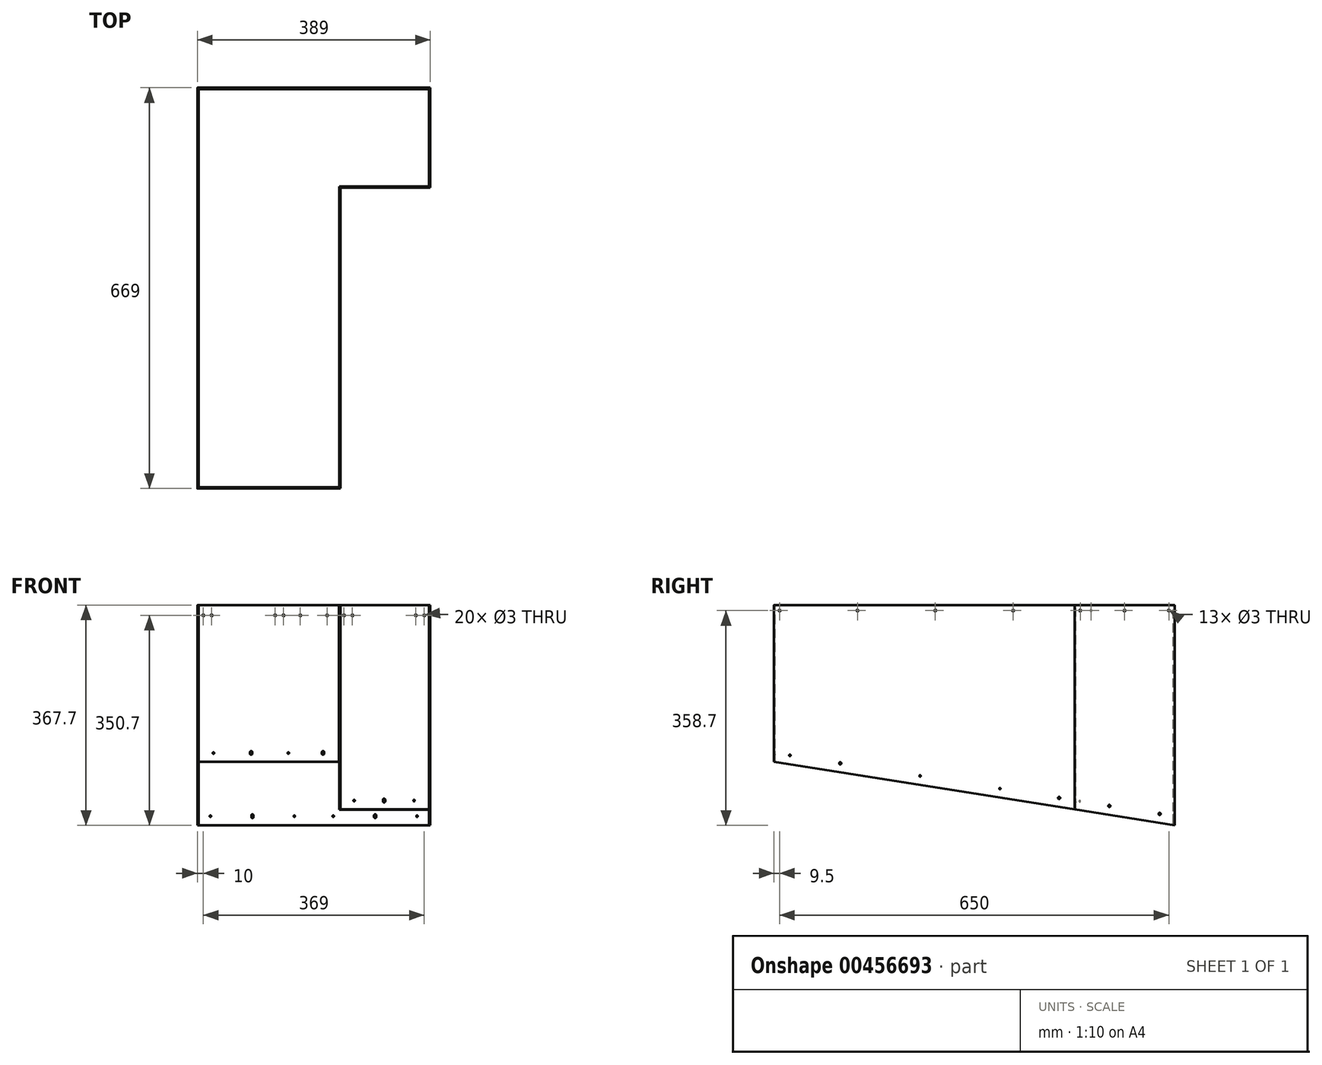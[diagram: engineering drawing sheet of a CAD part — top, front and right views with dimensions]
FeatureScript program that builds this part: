
annotation { "Feature Type Name" : "Feature", "Feature Type Description" : "" }
export const myFeature = defineFeature(function(context is Context, id is Id, definition is map)
    precondition{}
    {
        {
            var Q0;
            Q0=qCreatedBy(makeId("Top.planeOp"),FACE);
            var sketch = newSketch(context, id + "F0", { "sketchPlane" : qUnion([Q0])});
            skLineSegment(sketch, "E0.bottom", {"start": v(192.25, 332.5) * mm, "end": v(-192.25, 332.5) * mm});
            skLineSegment(sketch, "E0.top", {"start": v(192.25, 334.5) * mm, "end": v(-192.25, 334.5) * mm});
            skLineSegment(sketch, "E0.left", {"start": v(192.25, 332.5) * mm, "end": v(192.25, 334.5) * mm});
            skLineSegment(sketch, "E0.right", {"start": v(-192.25, 332.5) * mm, "end": v(-192.25, 334.5) * mm});
            skPoint(sketch, "E0.middle", {"position": v(0, 333.5) * mm});
            skSolve(sketch);
        }
        {
            var Q0;
            Q0=qSketchRegion(id+"F0",true);
            extrude(context, id + "F1", {"entities" : qUnion([Q0]), "oppositeDirection" : true, "depth" : 367.4 * mm});
        }
        {
            var Q0;
            Q0=qCreatedBy(makeId("Top.planeOp"),FACE);
            var sketch = newSketch(context, id + "F2", { "sketchPlane" : qUnion([Q0])});
            skLineSegment(sketch, "E1.bottom", {"start": v(-192.25, -332.5) * mm, "end": v(42.25, -332.5) * mm});
            skLineSegment(sketch, "E1.top", {"start": v(-192.25, -334.5) * mm, "end": v(42.25, -334.5) * mm});
            skLineSegment(sketch, "E1.left", {"start": v(-192.25, -332.5) * mm, "end": v(-192.25, -334.5) * mm});
            skLineSegment(sketch, "E1.right", {"start": v(42.25, -332.5) * mm, "end": v(42.25, -334.5) * mm});
            skSolve(sketch);
        }
        {
            var Q0;
            Q0=qSketchRegion(id+"F2",true);
            extrude(context, id + "F3", {"entities" : qUnion([Q0]), "oppositeDirection" : true, "depth" : 261.8 * mm});
        }
        {
            var Q0;
            Q0=qCreatedBy(makeId("Top.planeOp"),FACE);
            var sketch = newSketch(context, id + "F4", { "sketchPlane" : qUnion([Q0])});
            skLineSegment(sketch, "E2.bottom", {"start": v(42.75, 169.5) * mm, "end": v(192.25, 169.5) * mm});
            skLineSegment(sketch, "E2.top", {"start": v(42.75, 167.5) * mm, "end": v(192.25, 167.5) * mm});
            skLineSegment(sketch, "E2.left", {"start": v(42.75, 169.5) * mm, "end": v(42.75, 167.5) * mm});
            skLineSegment(sketch, "E2.right", {"start": v(192.25, 169.5) * mm, "end": v(192.25, 167.5) * mm});
            skSolve(sketch);
        }
        {
            var Q0;
            Q0=qSketchRegion(id+"F4",true);
            extrude(context, id + "F5", {"entities" : qUnion([Q0]), "oppositeDirection" : true, "depth" : 341.3 * mm});
        }
        {
            var Q0;
            Q0=qCreatedBy(makeId("Top.planeOp"),FACE);
            var sketch = newSketch(context, id + "F6", { "sketchPlane" : qUnion([Q0])});
            skLineSegment(sketch, "E3.bottom", {"start": v(-192.5, -334.5) * mm, "end": v(-194.5, -334.5) * mm});
            skLineSegment(sketch, "E3.top", {"start": v(-192.5, 334.5) * mm, "end": v(-194.5, 334.5) * mm});
            skLineSegment(sketch, "E3.left", {"start": v(-192.5, -334.5) * mm, "end": v(-192.5, 334.5) * mm});
            skLineSegment(sketch, "E3.right", {"start": v(-194.5, -334.5) * mm, "end": v(-194.5, 334.5) * mm});
            skPoint(sketch, "E3.middle", {"position": v(-193.5, 0) * mm});
            skLineSegment(sketch, "E4.bottom", {"start": v(42.5, 167.5) * mm, "end": v(44.5, 167.5) * mm});
            skLineSegment(sketch, "E4.top", {"start": v(42.5, -334.5) * mm, "end": v(44.5, -334.5) * mm});
            skLineSegment(sketch, "E4.left", {"start": v(42.5, 167.5) * mm, "end": v(42.5, -334.5) * mm});
            skLineSegment(sketch, "E4.right", {"start": v(44.5, 167.5) * mm, "end": v(44.5, -334.5) * mm});
            skLineSegment(sketch, "E5.bottom", {"start": v(192.5, 334.5) * mm, "end": v(194.5, 334.5) * mm});
            skLineSegment(sketch, "E5.top", {"start": v(192.5, 167.5) * mm, "end": v(194.5, 167.5) * mm});
            skLineSegment(sketch, "E5.left", {"start": v(192.5, 334.5) * mm, "end": v(192.5, 167.5) * mm});
            skLineSegment(sketch, "E5.right", {"start": v(194.5, 334.5) * mm, "end": v(194.5, 167.5) * mm});
            skSolve(sketch);
        }
        {
            var Q0;
            Q0=qSketchRegion(id+"F6",true);
            extrude(context, id + "F7", {"entities" : qUnion([Q0]), "oppositeDirection" : true, "depth" : 388 * mm});
        }
        {
            var Q0;
            Q0=makeQuery(id+"F1.opExtrude","SWEPT_FACE",FACE,{"disambiguationData":[OSD([sQuery(id+"F0.wireOp",EDGE,"E0.top")])]});
            var sketch = newSketch(context, id + "F8", { "sketchPlane" : qUnion([Q0])});
            skCircle(sketch, "E6", {"center": v(184.5, -17) * mm, "radius": 1.5 * mm});
            skCircle(sketch, "E7", {"center": v(170.5, -17) * mm, "radius": 1.5 * mm});
            skCircle(sketch, "E8", {"center": v(64.5, -17) * mm, "radius": 1.5 * mm});
            skCircle(sketch, "E9", {"center": v(50.5, -17) * mm, "radius": 1.5 * mm});
            skCircle(sketch, "E10.1.0.0", {"center": v(-64.5, -17) * mm, "radius": 1.5 * mm});
            skCircle(sketch, "E10.1.0.1", {"center": v(-50.5, -17) * mm, "radius": 1.5 * mm});
            skCircle(sketch, "E10.1.0.2", {"center": v(-184.5, -17) * mm, "radius": 1.5 * mm});
            skCircle(sketch, "E10.1.0.3", {"center": v(-170.5, -17) * mm, "radius": 1.5 * mm});
            skLineSegment(sketch, "E10.direction1", {"start": v(50.5, -17) * mm, "end": v(-184.5, -17) * mm, "construction": true});
            skCircle(sketch, "E11", {"center": v(22.5, -17) * mm, "radius": 1.5 * mm});
            skCircle(sketch, "E12", {"center": v(-22.3, -17) * mm, "radius": 1.5 * mm});
            skLineSegment(sketch, "E13", {"start": v(42.5, 7.75) * mm, "end": v(42.5, -58.99) * mm, "construction": true});
            skCircle(sketch, "E14", {"center": v(102.5, -352.4) * mm, "radius": 1.75 * mm, "construction": true});
            skCircle(sketch, "E15", {"center": v(-102.5, -352.4) * mm, "radius": 1.75 * mm, "construction": true});
            skCircle(sketch, "E16", {"center": v(172.5, -352.4) * mm, "radius": 1.2 * mm});
            skCircle(sketch, "E17", {"center": v(-172.5, -352.4) * mm, "radius": 1.2 * mm});
            skCircle(sketch, "E18", {"center": v(-32.5, -352.4) * mm, "radius": 1.2 * mm});
            skCircle(sketch, "E19", {"center": v(32.5, -352.4) * mm, "radius": 1.2 * mm});
            skLineSegment(sketch, "E20.left", {"start": v(-100.75, -354.4) * mm, "end": v(-100.75, -350.4) * mm});
            skLineSegment(sketch, "E20.right", {"start": v(-104.25, -354.4) * mm, "end": v(-104.25, -350.4) * mm});
            skArc(sketch, "E21", {"start": v(-100.75, -350.4) * mm, "mid": v(-102.5, -349.37) * mm, "end": v(-104.25, -350.4) * mm});
            skArc(sketch, "E22", {"start": v(-104.25, -354.4) * mm, "mid": v(-102.5, -355.43) * mm, "end": v(-100.75, -354.4) * mm});
            skLineSegment(sketch, "E23.left", {"start": v(104.25, -354.4) * mm, "end": v(104.25, -350.4) * mm});
            skLineSegment(sketch, "E23.right", {"start": v(100.75, -354.4) * mm, "end": v(100.75, -350.4) * mm});
            skArc(sketch, "E24", {"start": v(104.25, -350.4) * mm, "mid": v(102.5, -349.37) * mm, "end": v(100.75, -350.4) * mm});
            skArc(sketch, "E25", {"start": v(100.75, -354.4) * mm, "mid": v(102.5, -355.43) * mm, "end": v(104.25, -354.4) * mm});
            skLineSegment(sketch, "E26", {"start": v(-192.5, 1.16) * mm, "end": v(192.5, 1.16) * mm, "construction": true});
            skSolve(sketch);
        }
        {
            var Q0;
            Q0=qSketchRegion(id+"F8",true);
            extrude(context, id + "F9", {"entities" : qUnion([Q0]), "operationType" : NewBodyOperationType.REMOVE, "oppositeDirection" : true, "depth" : 2 * mm});
        }
        {
            var Q0;
            Q0=makeQuery(id+"F3.opExtrude","SWEPT_FACE",FACE,{"disambiguationData":[OSD([sQuery(id+"F2.wireOp",EDGE,"E1.top")])]});
            var sketch = newSketch(context, id + "F10", { "sketchPlane" : qUnion([Q0])});
            skCircle(sketch, "E27", {"center": v(-184.5, -17) * mm, "radius": 1.5 * mm});
            skCircle(sketch, "E28", {"center": v(-170.5, -17) * mm, "radius": 1.5 * mm});
            skCircle(sketch, "E29.1.0.0", {"center": v(-64.5, -17) * mm, "radius": 1.5 * mm});
            skCircle(sketch, "E29.1.0.1", {"center": v(-50.5, -17) * mm, "radius": 1.5 * mm});
            skCircle(sketch, "E30.1.0.0", {"center": v(-22.5, -17) * mm, "radius": 1.5 * mm});
            skCircle(sketch, "E30.1.0.1", {"center": v(22.3, -17) * mm, "radius": 1.5 * mm});
            skCircle(sketch, "E31", {"center": v(-104.5, -246.8) * mm, "radius": 1.75 * mm, "construction": true});
            skCircle(sketch, "E32", {"center": v(15.5, -246.8) * mm, "radius": 1.75 * mm, "construction": true});
            skCircle(sketch, "E33", {"center": v(-167.5, -246.8) * mm, "radius": 1.2 * mm});
            skCircle(sketch, "E34", {"center": v(-42.5, -246.8) * mm, "radius": 1.2 * mm});
            skLineSegment(sketch, "E35.left", {"start": v(-102.75, -248.8) * mm, "end": v(-102.75, -244.8) * mm});
            skLineSegment(sketch, "E35.right", {"start": v(-106.25, -248.8) * mm, "end": v(-106.25, -244.8) * mm});
            skArc(sketch, "E36", {"start": v(-102.75, -244.8) * mm, "mid": v(-104.5, -243.77) * mm, "end": v(-106.25, -244.8) * mm});
            skArc(sketch, "E37", {"start": v(-106.25, -248.8) * mm, "mid": v(-104.5, -249.83) * mm, "end": v(-102.75, -248.8) * mm});
            skLineSegment(sketch, "E38.left", {"start": v(17.25, -248.8) * mm, "end": v(17.25, -244.8) * mm});
            skLineSegment(sketch, "E38.right", {"start": v(13.75, -248.8) * mm, "end": v(13.75, -244.8) * mm});
            skArc(sketch, "E39", {"start": v(17.25, -244.8) * mm, "mid": v(15.5, -243.77) * mm, "end": v(13.75, -244.8) * mm});
            skArc(sketch, "E40", {"start": v(13.75, -248.8) * mm, "mid": v(15.5, -249.83) * mm, "end": v(17.25, -248.8) * mm});
            skLineSegment(sketch, "E41", {"start": v(-192.5, 3.66) * mm, "end": v(42.5, 3.66) * mm, "construction": true});
            skSolve(sketch);
        }
        {
            var Q0;
            Q0=qSketchRegion(id+"F10",true);
            extrude(context, id + "F11", {"entities" : qUnion([Q0]), "operationType" : NewBodyOperationType.REMOVE, "oppositeDirection" : true, "depth" : 2 * mm});
        }
        {
            var Q0;
            Q0=makeQuery(id+"F7.opExtrude","SWEPT_FACE",FACE,{"disambiguationData":[OSD([sQuery(id+"F6.wireOp",EDGE,"E3.right")])]});
            var sketch = newSketch(context, id + "F12", { "sketchPlane" : qUnion([Q0])});
            skCircle(sketch, "E42", {"center": v(-325, -9) * mm, "radius": 1.5 * mm});
            skLineSegment(sketch, "E43", {"start": v(-334.5, -367.7) * mm, "end": v(334.5, -367.7) * mm});
            skLineSegment(sketch, "E44", {"start": v(-334.5, -367.7) * mm, "end": v(334.5, -261.74) * mm});
            skLineSegment(sketch, "E45", {"start": v(334.5, -261.74) * mm, "end": v(334.5, -367.7) * mm});
            skLineSegment(sketch, "E46", {"start": v(-334.5, -367.7) * mm, "end": v(-334.5, -388) * mm});
            skLineSegment(sketch, "E47", {"start": v(-334.5, -388) * mm, "end": v(334.5, -388) * mm});
            skLineSegment(sketch, "E48", {"start": v(334.5, -388) * mm, "end": v(334.5, -367.7) * mm});
            skCircle(sketch, "E49.1.0.0", {"center": v(-195, -9) * mm, "radius": 1.5 * mm});
            skCircle(sketch, "E49.2.0.0", {"center": v(-65, -9) * mm, "radius": 1.5 * mm});
            skCircle(sketch, "E49.3.0.0", {"center": v(65, -9) * mm, "radius": 1.5 * mm});
            skCircle(sketch, "E49.4.0.0", {"center": v(195, -9) * mm, "radius": 1.5 * mm});
            skCircle(sketch, "E49.5.0.0", {"center": v(325, -9) * mm, "radius": 1.5 * mm});
            skLineSegment(sketch, "E49.direction1", {"start": v(-325, -9) * mm, "end": v(-195, -9) * mm, "construction": true});
            skCircle(sketch, "E50", {"center": v(-309.59, -348.57) * mm, "radius": 1.75 * mm});
            skLineSegment(sketch, "E51", {"start": v(-334.5, -367.7) * mm, "end": v(-337.36, -349.64) * mm, "construction": true});
            skCircle(sketch, "E52", {"center": v(223.77, -264.1) * mm, "radius": 1.75 * mm});
            skCircle(sketch, "E53.1.0.0", {"center": v(-176.25, -327.45) * mm, "radius": 1.75 * mm, "construction": true});
            skCircle(sketch, "E53.2.0.0", {"center": v(-42.91, -306.33) * mm, "radius": 1.75 * mm, "construction": true});
            skLineSegment(sketch, "E53.direction1", {"start": v(-309.59, -348.57) * mm, "end": v(-176.25, -327.45) * mm, "construction": true});
            skCircle(sketch, "E54.0.3.0", {"center": v(90.43, -285.21) * mm, "radius": 1.75 * mm, "construction": true});
            skCircle(sketch, "E55", {"center": v(307.72, -250.8) * mm, "radius": 1.2 * mm});
            skCircle(sketch, "E56", {"center": v(-176.25, -327.45) * mm, "radius": 1.2 * mm});
            skCircle(sketch, "E57", {"center": v(-42.91, -306.33) * mm, "radius": 1.2 * mm});
            skCircle(sketch, "E58", {"center": v(90.43, -285.21) * mm, "radius": 1.2 * mm});
            skSolve(sketch);
        }
        {
            var Q0;
            Q0=qSketchRegion(id+"F12",true);
            extrude(context, id + "F13", {"entities" : qUnion([Q0]), "operationType" : NewBodyOperationType.REMOVE, "oppositeDirection" : true, "depth" : 2 * mm});
        }
        {
            var Q0;
            Q0=makeQuery(id+"F12.imprint","IMPRINT",FACE,{"disambiguationData":[TD([[makeQuery(id+"F12.imprint","IMPRINT",EDGE,{"derivedFrom":sQuery(id+"F12.wireOp",EDGE,"E43")}),-1.0]])]});
            var Q1;
            Q1=makeQuery(id+"F12.imprint","IMPRINT",FACE,{"disambiguationData":[TD([[makeQuery(id+"F12.imprint","IMPRINT",EDGE,{"derivedFrom":sQuery(id+"F12.wireOp",EDGE,"E43")}),1.0]])]});
            extrude(context, id + "F14", {"entities" : qUnion([Q0, Q1]), "operationType" : NewBodyOperationType.REMOVE, "oppositeDirection" : true, "depth" : 428 * mm});
        }
        {
            var Q0;
            Q0=makeQuery(id+"F7.opExtrude","SWEPT_FACE",FACE,{"disambiguationData":[OSD([sQuery(id+"F6.wireOp",EDGE,"E5.right")])]});
            var sketch = newSketch(context, id + "F15", { "sketchPlane" : qUnion([Q0])});
            skCircle(sketch, "E59", {"center": v(325, -9) * mm, "radius": 1.5 * mm});
            skCircle(sketch, "E60.1.0.0", {"center": v(251, -9) * mm, "radius": 1.5 * mm});
            skCircle(sketch, "E60.2.0.0", {"center": v(177, -9) * mm, "radius": 1.5 * mm});
            skLineSegment(sketch, "E60.direction1", {"start": v(325, -9) * mm, "end": v(251, -9) * mm, "construction": true});
            skCircle(sketch, "E61", {"center": v(309.59, -348.57) * mm, "radius": 1.75 * mm});
            skCircle(sketch, "E62", {"center": v(225.63, -335.27) * mm, "radius": 1.75 * mm});
            skSolve(sketch);
        }
        {
            var Q0;
            Q0=qSketchRegion(id+"F15",true);
            extrude(context, id + "F16", {"entities" : qUnion([Q0]), "operationType" : NewBodyOperationType.REMOVE, "oppositeDirection" : true, "depth" : 2 * mm});
        }
        {
            var Q0;
            Q0=makeQuery(id+"F5.opExtrude","SWEPT_FACE",FACE,{"disambiguationData":[OSD([sQuery(id+"F4.wireOp",EDGE,"E2.top")])]});
            var sketch = newSketch(context, id + "F17", { "sketchPlane" : qUnion([Q0])});
            skCircle(sketch, "E63", {"center": v(50.5, -17) * mm, "radius": 1.5 * mm});
            skCircle(sketch, "E64", {"center": v(64.5, -17) * mm, "radius": 1.5 * mm});
            skCircle(sketch, "E65", {"center": v(170.5, -17) * mm, "radius": 1.5 * mm});
            skCircle(sketch, "E66", {"center": v(184.5, -17) * mm, "radius": 1.5 * mm});
            skCircle(sketch, "E67", {"center": v(117.5, -326.3) * mm, "radius": 1.75 * mm, "construction": true});
            skCircle(sketch, "E68", {"center": v(67.5, -326.3) * mm, "radius": 1.2 * mm});
            skCircle(sketch, "E69", {"center": v(167.5, -326.3) * mm, "radius": 1.2 * mm});
            skLineSegment(sketch, "E70.left", {"start": v(119.25, -328.3) * mm, "end": v(119.25, -324.3) * mm});
            skLineSegment(sketch, "E70.right", {"start": v(115.75, -328.3) * mm, "end": v(115.75, -324.3) * mm});
            skArc(sketch, "E71", {"start": v(119.25, -324.3) * mm, "mid": v(117.5, -323.27) * mm, "end": v(115.75, -324.3) * mm});
            skArc(sketch, "E72", {"start": v(115.75, -328.3) * mm, "mid": v(117.5, -329.33) * mm, "end": v(119.25, -328.3) * mm});
            skSolve(sketch);
        }
        {
            var Q0;
            Q0=qSketchRegion(id+"F17",true);
            extrude(context, id + "F18", {"entities" : qUnion([Q0]), "operationType" : NewBodyOperationType.REMOVE, "oppositeDirection" : true, "depth" : 2 * mm});
        }
        {
            var Q0;
            Q0=makeQuery(id+"F7.opExtrude","SWEPT_FACE",FACE,{"disambiguationData":[OSD([sQuery(id+"F6.wireOp",EDGE,"E4.right")])]});
            var sketch = newSketch(context, id + "F19", { "sketchPlane" : qUnion([Q0])});
            skCircle(sketch, "E73", {"center": v(-325, -9) * mm, "radius": 1.5 * mm});
            skCircle(sketch, "E74.1.0.0", {"center": v(-195, -9) * mm, "radius": 1.5 * mm});
            skCircle(sketch, "E74.2.0.0", {"center": v(-65, -9) * mm, "radius": 1.5 * mm});
            skCircle(sketch, "E74.3.0.0", {"center": v(65, -9) * mm, "radius": 1.5 * mm});
            skCircle(sketch, "E74.4.0.0", {"center": v(195, -9) * mm, "radius": 1.5 * mm});
            skCircle(sketch, "E74.5.0.0", {"center": v(325, -9) * mm, "radius": 1.5 * mm});
            skLineSegment(sketch, "E74.direction1", {"start": v(-325, -9) * mm, "end": v(-195, -9) * mm, "construction": true});
            skPoint(sketch, "E75.0", {"position": v(-307.72, -250.8) * mm});
            skPoint(sketch, "E75.1", {"position": v(-223.77, -264.1) * mm});
            skPoint(sketch, "E75.2", {"position": v(-90.43, -285.21) * mm});
            skCircle(sketch, "E76", {"center": v(-223.77, -264.1) * mm, "radius": 1.75 * mm});
            skCircle(sketch, "E77", {"center": v(-307.72, -250.8) * mm, "radius": 1.2 * mm});
            skCircle(sketch, "E78", {"center": v(-90.43, -285.21) * mm, "radius": 1.2 * mm});
            skPoint(sketch, "E79.0", {"position": v(42.91, -306.33) * mm});
            skCircle(sketch, "E80", {"center": v(42.91, -306.33) * mm, "radius": 1.2 * mm});
            skCircle(sketch, "E81", {"center": v(141.68, -321.97) * mm, "radius": 1.75 * mm});
            skSolve(sketch);
        }
        {
            var Q0;
            Q0=qSketchRegion(id+"F19",true);
            extrude(context, id + "F20", {"entities" : qUnion([Q0]), "operationType" : NewBodyOperationType.REMOVE, "oppositeDirection" : true, "depth" : 2 * mm});
        }
        {
            var Q0;
            Q0=makeQuery(id+"F7.opExtrude","CAP_EDGE",EDGE,{"disambiguationData":[OSD([sQuery(id+"F6.wireOp",EDGE,"E3.top")])],"isStart":true});
            var Q1;
            Q1=makeQuery(id+"F7.opExtrude","CAP_EDGE",EDGE,{"disambiguationData":[OSD([sQuery(id+"F6.wireOp",EDGE,"E3.bottom")])],"isStart":true});
            var Q2;
            Q2=makeQuery(id+"F7.opExtrude","CAP_EDGE",EDGE,{"disambiguationData":[OSD([sQuery(id+"F6.wireOp",EDGE,"E5.bottom")])],"isStart":true});
            var Q3;
            Q3=makeQuery(id+"F7.opExtrude","CAP_EDGE",EDGE,{"disambiguationData":[OSD([sQuery(id+"F6.wireOp",EDGE,"E5.top")])],"isStart":true});
            var Q4;
            Q4=makeQuery(id+"F5.opExtrude","CAP_EDGE",EDGE,{"disambiguationData":[OSD([sQuery(id+"F4.wireOp",EDGE,"E2.right")])],"isStart":true});
            var Q5;
            Q5=makeQuery(id+"F5.opExtrude","CAP_EDGE",EDGE,{"disambiguationData":[OSD([sQuery(id+"F4.wireOp",EDGE,"E2.left")])],"isStart":true});
            var Q6;
            Q6=makeQuery(id+"F1.opExtrude","CAP_EDGE",EDGE,{"disambiguationData":[OSD([sQuery(id+"F0.wireOp",EDGE,"E0.left")])],"isStart":true});
            var Q7;
            Q7=makeQuery(id+"F1.opExtrude","CAP_EDGE",EDGE,{"disambiguationData":[OSD([sQuery(id+"F0.wireOp",EDGE,"E0.right")])],"isStart":true});
            var Q8;
            Q8=makeQuery(id+"F7.opExtrude","CAP_EDGE",EDGE,{"disambiguationData":[OSD([sQuery(id+"F6.wireOp",EDGE,"E4.top")])],"isStart":true});
            var Q9;
            Q9=makeQuery(id+"F7.opExtrude","CAP_EDGE",EDGE,{"disambiguationData":[OSD([sQuery(id+"F6.wireOp",EDGE,"E4.bottom")])],"isStart":true});
            var Q10;
            Q10=makeQuery(id+"F3.opExtrude","CAP_EDGE",EDGE,{"disambiguationData":[OSD([sQuery(id+"F2.wireOp",EDGE,"E1.right")])],"isStart":true});
            var Q11;
            Q11=makeQuery(id+"F3.opExtrude","CAP_EDGE",EDGE,{"disambiguationData":[OSD([sQuery(id+"F2.wireOp",EDGE,"E1.left")])],"isStart":true});
            fillet(context, id + "F21", {"entities" : qUnion([Q0, Q1, Q2, Q3, Q4, Q5, Q6, Q7, Q8, Q9, Q10, Q11]), "radius" : 1 * mm, "tangentPropagation" : true, "allowEdgeOverflow" : false});
        }
    });
